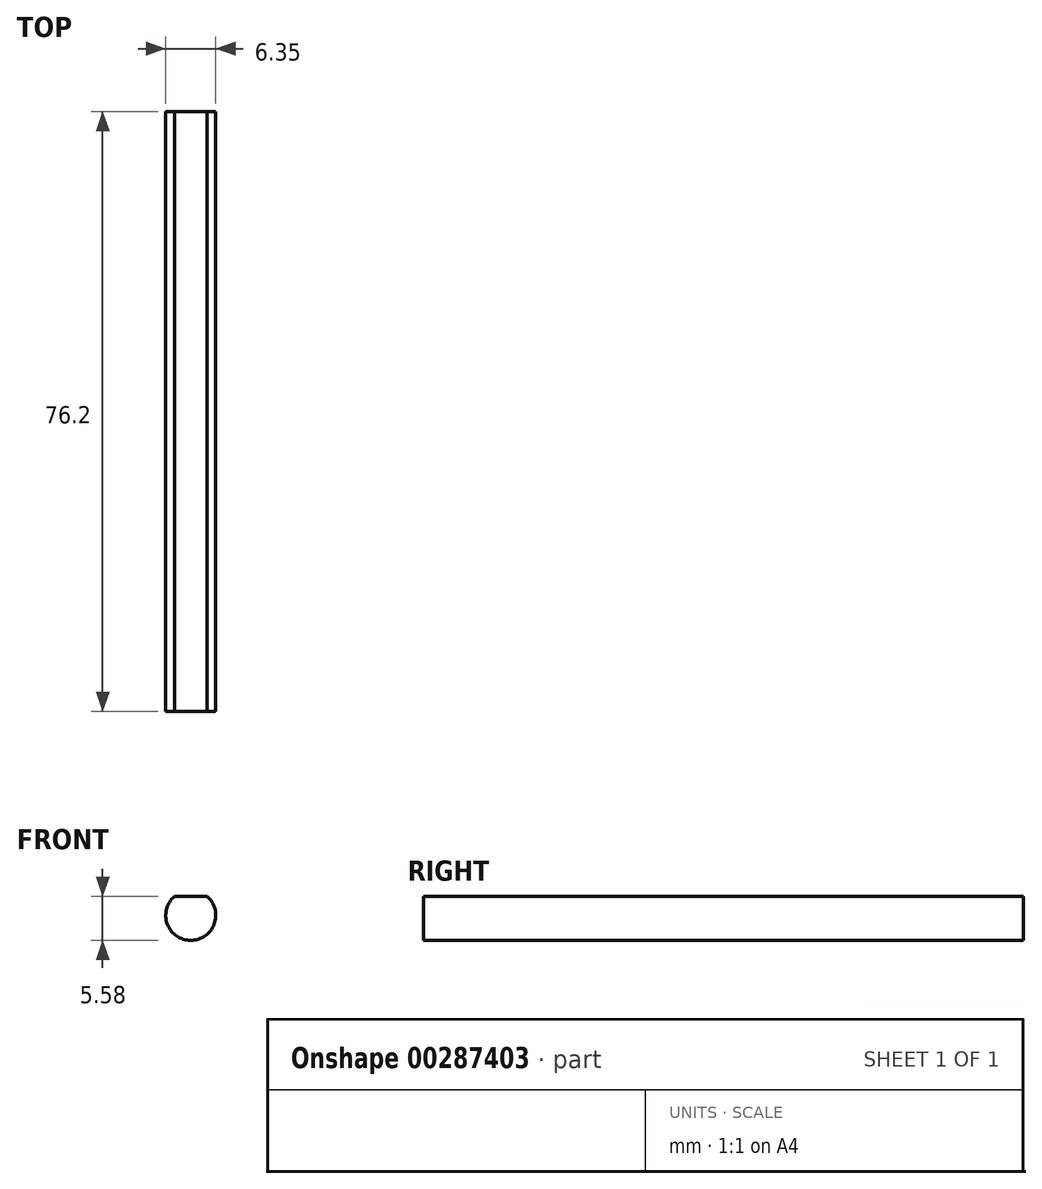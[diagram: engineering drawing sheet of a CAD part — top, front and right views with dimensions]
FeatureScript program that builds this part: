
annotation { "Feature Type Name" : "Feature", "Feature Type Description" : "" }
export const myFeature = defineFeature(function(context is Context, id is Id, definition is map)
    precondition{}
    {
        {
            var Q0;
            Q0=qCreatedBy(makeId("Front.planeOp"),FACE);
            var sketch = newSketch(context, id + "F0", { "sketchPlane" : qUnion([Q0])});
            skCircle(sketch, "E0", {"center": v(0, 0) * mm, "radius": 3.18 * mm});
            skLineSegment(sketch, "E1.bottom", {"start": v(-8.93, -4.24) * mm, "end": v(11.49, -4.24) * mm});
            skLineSegment(sketch, "E1.top", {"start": v(-8.93, 2.41) * mm, "end": v(11.49, 2.41) * mm});
            skLineSegment(sketch, "E1.left", {"start": v(-8.93, -4.24) * mm, "end": v(-8.93, 2.41) * mm});
            skLineSegment(sketch, "E1.right", {"start": v(11.49, -4.24) * mm, "end": v(11.49, 2.41) * mm});
            skSolve(sketch);
        }
        {
            var Q0;
            {var subQ0=sQuery(id+"F0.wireOp",EDGE,"E1.top");var subQ1=sQuery(id+"F0.wireOp",EDGE,"E0");var subQ2=makeQuery(id+"F0.imprint","INTERSECT",VERTEX,{"disambiguationData":[OD(0.0)],"derivedFrom":[subQ1,subQ0]});Q0=makeQuery(id+"F0.imprint","IMPRINT",FACE,{"disambiguationData":[TD([[makeQuery(id+"F0.imprint","IMPRINT",EDGE,{"disambiguationData":[TD([[subQ2,-1.0]])],"derivedFrom":subQ1}),1.0]])]});}
            extrude(context, id + "F1", {"entities" : qUnion([Q0]), "depth" : 76.2 * mm});
        }
    });
